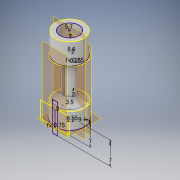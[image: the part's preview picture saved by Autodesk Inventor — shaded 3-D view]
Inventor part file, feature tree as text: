
AUTODESK INVENTOR PART (.ipt)
format: ipt  version: 2019.3 (Build 233278000, 278)  size: 186,880 bytes
history: native  units: in
note: dims shown in document units (in); Inventor stores cm internally (conversion verified against a paired STEP export)
features: sketch x6, extrude x6, other x4, projected_geometry x3, fillet x1
ambient origin geometry x8: Origin, YZ Plane, XZ Plane, XY Plane, X Axis, Y Axis, Z Axis, Center Point
bodies: Body1 (feature_tree)
feature tree (20):
  other  "ソリッド1"
  sketch  "スケッチ2"
  sketch  "スケッチ1"
  extrude  "押し出し1"  Depth=0.0866in
  extrude  "押し出し2"  Depth=0.0217in
  other  "作業平面2"
  sketch  "スケッチ4"
  sketch  "スケッチ3"
  extrude  "押し出し6"  Depth=0.1969in TaperAngle=0.0deg
  other  "作業平面3"
  sketch  "スケッチ5"
  extrude  "押し出し8"  Depth=0.1181in TaperAngle=0.0deg
  sketch  "スケッチ7"
  extrude  "押し出し9"  Depth=0.3543in
  other  "作業平面4"
  extrude  "押し出し10"  Depth=0.1378in
  fillet  "フィレット3"  Radius=0.2756in
  projected_geometry  "投影ループ1"
  projected_geometry  "投影ループ2"
  projected_geometry  "投影ループ3"
